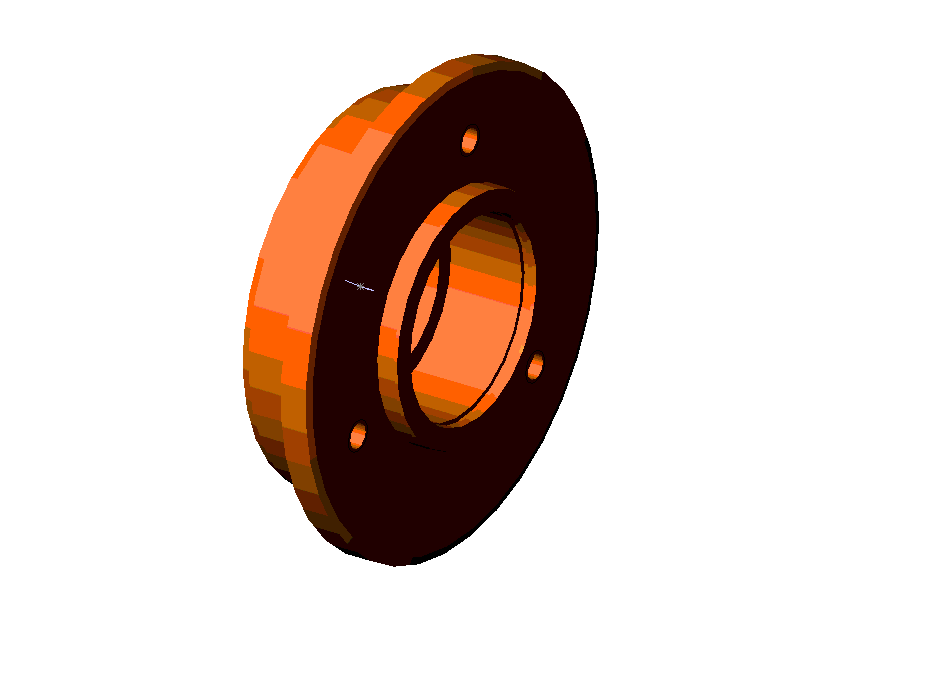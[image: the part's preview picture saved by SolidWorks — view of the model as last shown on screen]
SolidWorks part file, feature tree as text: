
SOLIDWORKS PART (.sldprt)
format: sldprt  version: not decoded by parser v0  size: 163,328 bytes
history: native  units: mm
features: plane x3, sketch x3, chamfer x3, material x1, revolve x1, hole x1, thread x1, pattern_circular x1 (+10 scaffold rows collapsed)
feature tree (24):
  scaffold x10  (default folders/planes/origin — collapsed)
  material  "Matériau <non spécifié>"
  plane  "Plan1"
  plane  "Plan2"
  plane  "Plan3"
  sketch  "Esquisse1"  dims[D1=1.0mm D2=1.0mm D3=5.0mm D4=0.5mm D5=6.0mm D6=4.75mm D7=1.9mm D8=7.0mm D9=10.61mm D10=13.0mm D11=13.6mm D12=16.0mm D13=30.5mm D14=24.7mm]
  revolve  "Base-Révolution"  Angle=360deg
  chamfer  "Chanfrein1"  Distance=0.5mm Angle=15deg
  chamfer  "Chanfrein2"  Distance=0.2mm Angle=15deg
  chamfer  "Chanfrein3"  Distance=0.5mm Angle=15deg
  hole  "Perçage1"  Diameter=1.6mm Depth=5.5mm
  sketch  "Esquisse3"  dims[D1=10.75mm]
  sketch  "Esquisse2"  dims[hole-wizard template sketch: 46 standard entries collapsed; hole parameters kept: c15.Diamètre du perçage=1.6mm c15.Profondeur du perçage=5.5mm c15.D3=~14.816244mm c15.Angle de pointe=118.0deg]
  thread  "Représentation de filetage1"  Diameter=3.5mm  [1 undecoded]
  pattern_circular  "Répétition circulaire1"  Count=3 Angle=120deg
decode coverage: 10 of 10 modeling features carry decoded parameters
note: ~ marks probable driven/reference dimensions
note: 1 parameter value undecoded
note: suppression state not decoded; provenance and decode notes live in map.json
